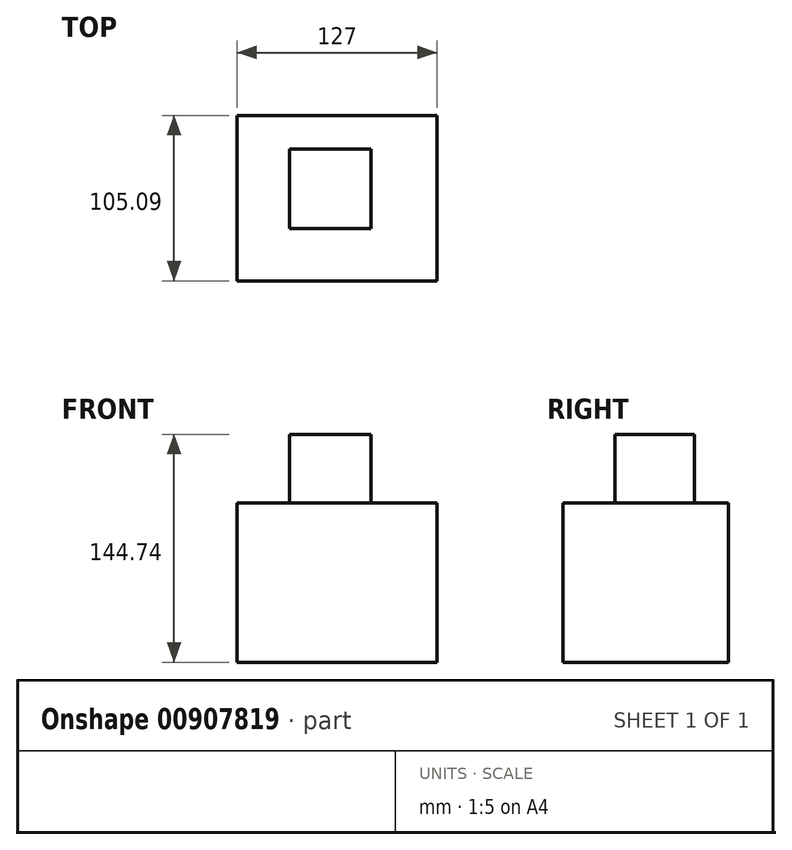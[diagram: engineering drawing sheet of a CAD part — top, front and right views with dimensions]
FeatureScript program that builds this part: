
annotation { "Feature Type Name" : "Feature", "Feature Type Description" : "" }
export const myFeature = defineFeature(function(context is Context, id is Id, definition is map)
    precondition{}
    {
        {
            var Q0;
            Q0=qCreatedBy(makeId("Top.planeOp"),FACE);
            var sketch = newSketch(context, id + "F0", { "sketchPlane" : qUnion([Q0])});
            skLineSegment(sketch, "E0.bottom", {"start": v(47.86, -52.9) * mm, "end": v(-53.74, -52.9) * mm});
            skLineSegment(sketch, "E0.top", {"start": v(47.86, 52.19) * mm, "end": v(-53.74, 52.19) * mm});
            skLineSegment(sketch, "E0.left", {"start": v(47.86, -52.9) * mm, "end": v(47.86, 52.19) * mm});
            skLineSegment(sketch, "E0.right", {"start": v(-53.74, -52.9) * mm, "end": v(-53.74, 52.19) * mm});
            skSolve(sketch);
        }
        {
            var Q0;
            Q0 = qSketchRegion(id + "F0", true);
            var Q1;
            Q1=makeQuery(id+"F0.imprint","IMPRINT",FACE,{"disambiguationData":[TD([[makeQuery(id+"F0.imprint","IMPRINT",EDGE,{"derivedFrom":sQuery(id+"F0.wireOp",EDGE,"E0.bottom")}),-1.0]])]});
            extrude(context, id + "F1", {"entities" : qUnion([Q0, Q1]), "depth" : 101.16 * mm, "offsetDistance" : 25.4 * mm});
        }
        {
            var Q0;
            Q0=makeQuery(id+"F1.opExtrude","SWEPT_FACE",FACE,{"disambiguationData":[OSD([sQuery(id+"F0.wireOp",EDGE,"E0.left")])]});
            var sketch = newSketch(context, id + "F2", { "sketchPlane" : qUnion([Q0])});
            skSolve(sketch);
        }
        {
            var Q0;
            {var subQ0=sQuery(id+"F0.wireOp",EDGE,"E0.left");Q0=makeQuery(id+"F2.imprint","IMPRINT",FACE,{"disambiguationData":[TD([[makeQuery(id+"F2.imprint","IMPRINT",EDGE,{"derivedFrom":makeQuery(id+"F1.opExtrude","CAP_EDGE",EDGE,{"disambiguationData":[OSD([subQ0])],"isStart":true})}),1.0]])]});}
            extrude(context, id + "F3", {"entities" : qUnion([Q0]), "operationType" : NewBodyOperationType.ADD, "depth" : 25.4 * mm, "offsetDistance" : 25.4 * mm});
        }
        {
            var Q0;
            {var subQ0=sQuery(id+"F0.wireOp",EDGE,"E0.bottom");Q0=makeQuery(id+"F3.boolean.opBoolean","MERGE",FACE,{"derivedFrom":[makeQuery(id+"F1.opExtrude","SWEPT_FACE",FACE,{"disambiguationData":[OSD([subQ0])]}),makeQuery(id+"F3.opExtrude","SWEPT_FACE",FACE,{"disambiguationData":[OSD([subQ0,sQuery(id+"F0.wireOp",EDGE,"E0.left")])]})]});}
            var sketch = newSketch(context, id + "F4", { "sketchPlane" : qUnion([Q0])});
            skCircle(sketch, "E1", {"center": v(9.6, 51.09) * mm, "radius": 26.28 * mm});
            skSolve(sketch);
        }
        {
            var Q0;
            Q0=sQuery(id+"F4.wireOp",EDGE,"E1");
            extrude(context, id + "F5", {"bodyType" : ToolBodyType.SURFACE, "surfaceEntities" : qUnion([Q0]), "depth" : 37.45 * mm, "offsetDistance" : 25.4 * mm});
        }
        {
            var Q0;
            {var subQ0=sQuery(id+"F0.wireOp",EDGE,"E0.left");Q0=makeQuery(id+"F3.boolean.opBoolean","MERGE",FACE,{"derivedFrom":[makeQuery(id+"F1.opExtrude","CAP_FACE",FACE,{"disambiguationData":[OSD([sQuery(id+"F0.wireOp",EDGE,"E0.bottom"),sQuery(id+"F0.wireOp",EDGE,"E0.top"),subQ0,sQuery(id+"F0.wireOp",EDGE,"E0.right")])],"isStart":false}),makeQuery(id+"F3.opExtrude","SWEPT_FACE",FACE,{"disambiguationData":[OSD([subQ0]),TDD([makeQuery(id+"F2.imprint","IMPRINT",EDGE,{"derivedFrom":makeQuery(id+"F1.opExtrude","CAP_EDGE",EDGE,{"disambiguationData":[OSD([subQ0])],"isStart":false})})])]})]});}
            var sketch = newSketch(context, id + "F6", { "sketchPlane" : qUnion([Q0])});
            skLineSegment(sketch, "E2.bottom", {"start": v(-20.52, -19.73) * mm, "end": v(31.33, -19.73) * mm});
            skLineSegment(sketch, "E2.top", {"start": v(-20.52, 30.64) * mm, "end": v(31.33, 30.64) * mm});
            skLineSegment(sketch, "E2.left", {"start": v(-20.52, -19.73) * mm, "end": v(-20.52, 30.64) * mm});
            skLineSegment(sketch, "E2.right", {"start": v(31.33, -19.73) * mm, "end": v(31.33, 30.64) * mm});
            skSolve(sketch);
        }
        {
            var Q0;
            Q0=makeQuery(id+"F6.imprint","IMPRINT",FACE,{"disambiguationData":[TD([[makeQuery(id+"F6.imprint","IMPRINT",EDGE,{"derivedFrom":sQuery(id+"F6.wireOp",EDGE,"E2.bottom")}),1.0]])]});
            extrude(context, id + "F7", {"entities" : qUnion([Q0]), "operationType" : NewBodyOperationType.ADD, "depth" : 43.58 * mm, "offsetDistance" : 25.4 * mm});
        }
    });
